# Revit family: 2
name_source: partatom
category: Casework
revit_build: Autodesk Revit Architecture 2012 (Build: 20110309_2315(x64)
units: mm (PartAtom-declared; Revit-internal decimal feet)

## types (1)
- As Specified
    Assembly Code = C1030410
    Construction Details = http://www.campbellrhea.com
    Depth = 1' - 11 3/4"
    Description = 18" Base Cabinet
    Door Finish = Frame - Maple
    Door Panel Material = Wood - Cherry
    Door Thickness = 0' - 1"
    DoorHeight = 6' - 7 1/2"
    DoorWidth = 3' - 4 3/4"
    Doors On = Yes
    Drawer Height_ Top = 0' - 5"
    Expected Lifespan (Years) = 0
    Frame Finish = Frame - Maple
    FrameReveal = 0' - 0 1/4"
    Glass Type = Wood - Pine
    Green Building-LEED = http://www.arcat.com
    Height = 7' - 0"
    Installation_Fabricaton = http://www.campbellrhea.com
    Keynote = 12 30 00
    Left Side Panel Finish = Frame - Maple
    Maintainence Schedule (Months) = 0
    Manufacturer = CampbellRhea
    Manufacturer Fax = 731-642-4262
    Manufacturer Website = http://www.campbellrhea.com
    Model = Generic Base Cabinet
    Panel Thickness = 0' - 0 3/4"
    Product Data = http://www.arcat.com
    Product Properties = http://www.campbellrhea.com
    Right Side Panel Finish = Frame - Maple
    Sales Information = http://www.campbellrhea.com
    Specification = http://www.arcat.com
    Toe Kick Depth = 0' - 2"
    Toe Kick Height = 0' - 4"
    Warranty Duration (Years) = 0
    Width = 3' - 5 1/4"

## geometry (parser evidence)
native form markers: Sweep x5
no freeform markers — native parametric forms only
